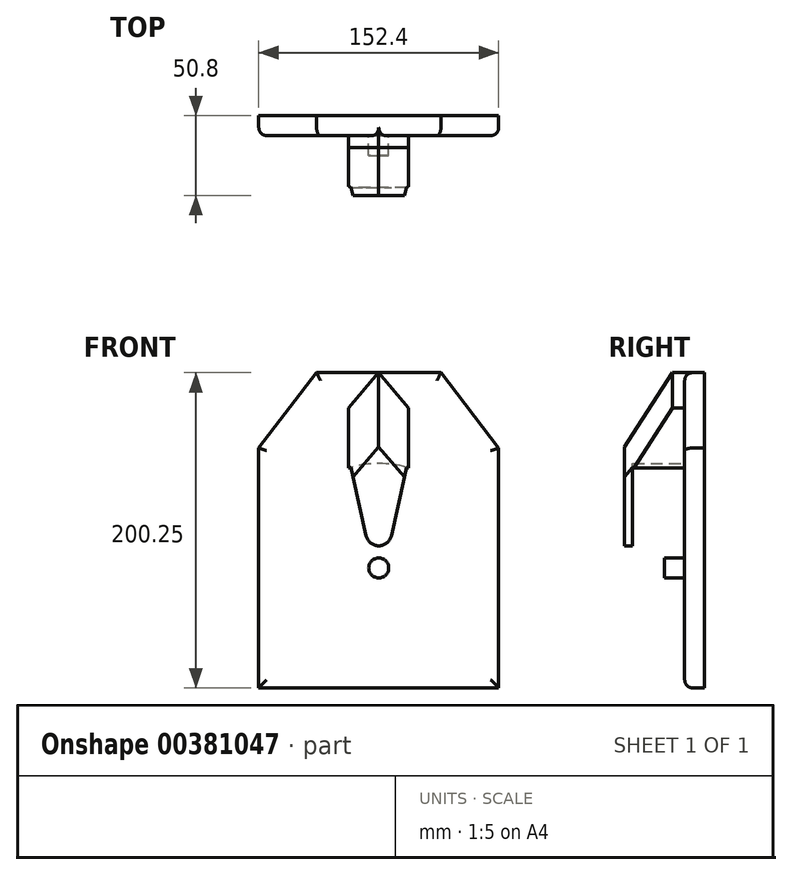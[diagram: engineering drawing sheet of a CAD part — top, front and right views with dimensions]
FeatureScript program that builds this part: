
annotation { "Feature Type Name" : "Feature", "Feature Type Description" : "" }
export const myFeature = defineFeature(function(context is Context, id is Id, definition is map)
    precondition{}
    {
        {
            var Q0;
            Q0=qCreatedBy(makeId("Front.planeOp"),FACE);
            var sketch = newSketch(context, id + "F0", { "sketchPlane" : qUnion([Q0])});
            skLineSegment(sketch, "E0.bottom", {"start": v(-76.2, 76.2) * mm, "end": v(76.2, 76.2) * mm});
            skLineSegment(sketch, "E0.top", {"start": v(-76.2, -76.2) * mm, "end": v(76.2, -76.2) * mm});
            skLineSegment(sketch, "E0.left", {"start": v(-76.2, 76.2) * mm, "end": v(-76.2, -76.2) * mm});
            skLineSegment(sketch, "E0.right", {"start": v(76.2, 76.2) * mm, "end": v(76.2, -76.2) * mm});
            skPoint(sketch, "E0.middle", {"position": v(0, 0) * mm});
            skLineSegment(sketch, "E1.bottom", {"start": v(-39.47, 124.05) * mm, "end": v(39.47, 124.05) * mm});
            skLineSegment(sketch, "E1.top", {"start": v(-39.47, 28.35) * mm, "end": v(39.47, 28.35) * mm});
            skLineSegment(sketch, "E1.left", {"start": v(-39.47, 124.05) * mm, "end": v(-39.47, 28.35) * mm});
            skLineSegment(sketch, "E1.right", {"start": v(39.47, 124.05) * mm, "end": v(39.47, 28.35) * mm});
            skPoint(sketch, "E1.middle", {"position": v(0, 76.2) * mm});
            skLineSegment(sketch, "E2", {"start": v(-39.47, 124.05) * mm, "end": v(-76.2, 76.2) * mm});
            skLineSegment(sketch, "E3", {"start": v(39.47, 124.05) * mm, "end": v(76.2, 76.2) * mm});
            skSolve(sketch);
        }
        {
            var Q0;
            Q0 = qSketchRegion(id + "F0", true);
            var Q1;
            {var subQ5=sQuery(id+"F0.wireOp",EDGE,"E1.top");Q1=makeQuery(id+"F0.imprint","IMPRINT",FACE,{"disambiguationData":[TD([[makeQuery(id+"F0.imprint","IMPRINT",EDGE,{"derivedFrom":subQ5}),1.0]])]});}
            extrude(context, id + "F1", {"entities" : qUnion([Q0, Q1]), "depth" : 12.7 * mm});
        }
        {
            var Q0;
            Q0=makeQuery(id+"F1.opExtrude","CAP_FACE",FACE,{"disambiguationData":[OSD([sQuery(id+"F0.wireOp",EDGE,"E0.bottom"),sQuery(id+"F0.wireOp",EDGE,"E0.top"),sQuery(id+"F0.wireOp",EDGE,"E0.left"),sQuery(id+"F0.wireOp",EDGE,"E0.right")])],"isStart":false});
            var sketch = newSketch(context, id + "F2", { "sketchPlane" : qUnion([Q0])});
            skCircle(sketch, "E4", {"center": v(0, 0) * mm, "radius": 6.35 * mm});
            skSolve(sketch);
        }
        {
            var Q0;
            Q0 = qSketchRegion(id + "F2", true);
            extrude(context, id + "F3", {"entities" : qUnion([Q0]), "operationType" : NewBodyOperationType.ADD, "depth" : 12.7 * mm});
        }
        {
            var Q0;
            Q0=makeQuery(id+"F1.opExtrude","CAP_FACE",FACE,{"disambiguationData":[OSD([sQuery(id+"F0.wireOp",EDGE,"E0.top"),sQuery(id+"F0.wireOp",EDGE,"E0.left"),sQuery(id+"F0.wireOp",EDGE,"E0.right"),sQuery(id+"F0.wireOp",EDGE,"E1.bottom"),sQuery(id+"F0.wireOp",EDGE,"E2"),sQuery(id+"F0.wireOp",EDGE,"E3")])],"isStart":false});
            var sketch = newSketch(context, id + "F4", { "sketchPlane" : qUnion([Q0])});
            skLineSegment(sketch, "E5.bottom", {"start": v(-19.05, 101.6) * mm, "end": v(19.05, 101.6) * mm});
            skLineSegment(sketch, "E5.top", {"start": v(-19.05, 63.5) * mm, "end": v(19.05, 63.5) * mm});
            skLineSegment(sketch, "E5.left", {"start": v(-19.05, 101.6) * mm, "end": v(-19.05, 63.5) * mm});
            skLineSegment(sketch, "E5.right", {"start": v(19.05, 101.6) * mm, "end": v(19.05, 63.5) * mm});
            skPoint(sketch, "E5.middle", {"position": v(0, 82.55) * mm});
            skLineSegment(sketch, "E6", {"start": v(0, 124.05) * mm, "end": v(19.05, 101.6) * mm});
            skLineSegment(sketch, "E7", {"start": v(0, 124.05) * mm, "end": v(-19.05, 101.6) * mm});
            skCircle(sketch, "E8", {"center": v(0, 0) * mm, "radius": 66.3 * mm});
            skSolve(sketch);
        }
        {
            var Q0;
            Q0=makeQuery(id+"F4.imprint","IMPRINT",FACE,{"disambiguationData":[TD([[makeQuery(id+"F4.imprint","IMPRINT",EDGE,{"derivedFrom":sQuery(id+"F4.wireOp",EDGE,"E5.bottom")}),1.0]])]});
            var Q1;
            Q1=makeQuery(id+"F4.imprint","IMPRINT",FACE,{"disambiguationData":[TD([[makeQuery(id+"F4.imprint","IMPRINT",EDGE,{"derivedFrom":sQuery(id+"F4.wireOp",EDGE,"E5.bottom")}),-1.0]])]});
            extrude(context, id + "F5", {"entities" : qUnion([Q0, Q1]), "operationType" : NewBodyOperationType.ADD, "depth" : 33.02 * mm});
        }
        {
            var Q0;
            Q0=makeQuery(id+"F5.opExtrude","CAP_EDGE",EDGE,{"disambiguationData":[OSD([sQuery(id+"F4.wireOp",EDGE,"E6")])],"isStart":false});
            var Q1;
            Q1=makeQuery(id+"F5.opExtrude","CAP_EDGE",EDGE,{"disambiguationData":[OSD([sQuery(id+"F4.wireOp",EDGE,"E7")])],"isStart":false});
            chamfer(context, id + "F6", {"entities" : qUnion([Q0, Q1]), "width" : 25.4 * mm, "tangentPropagation" : true});
        }
        {
            var Q0;
            Q0=makeQuery(id+"F5.opExtrude","CAP_FACE",FACE,{"disambiguationData":[OSD([sQuery(id+"F4.wireOp",EDGE,"E5.left"),sQuery(id+"F4.wireOp",EDGE,"E5.right"),sQuery(id+"F4.wireOp",EDGE,"E6"),sQuery(id+"F4.wireOp",EDGE,"E7"),sQuery(id+"F4.wireOp",EDGE,"E8")])],"isStart":false});
            var sketch = newSketch(context, id + "F7", { "sketchPlane" : qUnion([Q0])});
            skCircle(sketch, "E9", {"center": v(0, 22.23) * mm, "radius": 8.15 * mm});
            skPoint(sketch, "E9.centerSnap0", {"position": v(0, 66.3) * mm});
            skLineSegment(sketch, "E10", {"start": v(-17.75, 63.88) * mm, "end": v(-7.95, 20.43) * mm});
            skLineSegment(sketch, "E11", {"start": v(17.75, 63.88) * mm, "end": v(7.95, 20.43) * mm});
            skSolve(sketch);
        }
        {
            var Q0;
            Q0 = qSketchRegion(id + "F7", true);
            var Q1;
            {var subQ0=sQuery(id+"F7.wireOp",EDGE,"E10");Q1=makeQuery(id+"F7.imprint","IMPRINT",FACE,{"disambiguationData":[TD([[makeQuery(id+"F7.imprint","IMPRINT",EDGE,{"derivedFrom":subQ0}),1.0]])]});}
            var Q2;
            {var subQ0=sQuery(id+"F4.wireOp",EDGE,"E8");Q2=makeQuery(id+"F7.imprint","IMPRINT",FACE,{"disambiguationData":[TD([[makeQuery(id+"F7.imprint","IMPRINT",EDGE,{"derivedFrom":makeQuery(id+"F5.opExtrude","CAP_EDGE",EDGE,{"disambiguationData":[OSD([subQ0])],"isStart":false})}),-1.0]])]});}
            extrude(context, id + "F8", {"entities" : qUnion([Q0, Q1, Q2]), "operationType" : NewBodyOperationType.ADD, "depth" : 5.08 * mm});
        }
        {
            var Q0;
            {var subQ0=sQuery(id+"F4.wireOp",EDGE,"E8");var subQ1=sQuery(id+"F4.wireOp",EDGE,"E7");var subQ2=sQuery(id+"F4.wireOp",EDGE,"E6");var subQ3=sQuery(id+"F4.wireOp",EDGE,"E5.right");var subQ4=sQuery(id+"F4.wireOp",EDGE,"E5.left");Q0=makeQuery(id+"F8.opExtrude","CAP_EDGE",EDGE,{"disambiguationData":[OSD([subQ4,subQ3,subQ2,subQ1,subQ0]),TDD([makeQuery(id+"F7.imprint","IMPRINT",EDGE,{"derivedFrom":makeQuery(id+"F6.opChamfer","BLEND_EDGE",EDGE,{"blendedFrom":[makeQuery(id+"F5.opExtrude","CAP_EDGE",EDGE,{"disambiguationData":[OSD([subQ2])],"isStart":false}),makeQuery(id+"F5.opExtrude","CAP_FACE",FACE,{"disambiguationData":[OSD([subQ4,subQ3,subQ2,subQ1,subQ0])],"isStart":false})],"blendedInto":[makeQuery(id+"F5.opExtrude","CAP_FACE",FACE,{"disambiguationData":[OSD([subQ4,subQ3,subQ2,subQ1,subQ0])],"isStart":false})]})})])],"isStart":false});}
            var Q1;
            {var subQ0=sQuery(id+"F4.wireOp",EDGE,"E8");var subQ1=sQuery(id+"F4.wireOp",EDGE,"E7");var subQ2=sQuery(id+"F4.wireOp",EDGE,"E6");var subQ3=sQuery(id+"F4.wireOp",EDGE,"E5.right");var subQ4=sQuery(id+"F4.wireOp",EDGE,"E5.left");Q1=makeQuery(id+"F8.opExtrude","CAP_EDGE",EDGE,{"disambiguationData":[OSD([subQ4,subQ3,subQ2,subQ1,subQ0]),TDD([makeQuery(id+"F7.imprint","IMPRINT",EDGE,{"derivedFrom":makeQuery(id+"F6.opChamfer","BLEND_EDGE",EDGE,{"blendedFrom":[makeQuery(id+"F5.opExtrude","CAP_EDGE",EDGE,{"disambiguationData":[OSD([subQ1])],"isStart":false}),makeQuery(id+"F5.opExtrude","CAP_FACE",FACE,{"disambiguationData":[OSD([subQ4,subQ3,subQ2,subQ1,subQ0])],"isStart":false})],"blendedInto":[makeQuery(id+"F5.opExtrude","CAP_FACE",FACE,{"disambiguationData":[OSD([subQ4,subQ3,subQ2,subQ1,subQ0])],"isStart":false})]})})])],"isStart":false});}
            var Q2;
            Q2=makeQuery(id+"F5.opExtrude","CAP_EDGE",EDGE,{"disambiguationData":[OSD([sQuery(id+"F4.wireOp",EDGE,"E8")])],"isStart":false});
            chamfer(context, id + "F9", {"entities" : qUnion([Q0, Q1, Q2]), "width" : 5.08 * mm, "tangentPropagation" : true});
        }
        {
            var Q0;
            Q0=makeQuery(id+"F1.opExtrude","CAP_EDGE",EDGE,{"disambiguationData":[OSD([sQuery(id+"F0.wireOp",EDGE,"E3")])],"isStart":false});
            var Q1;
            Q1=makeQuery(id+"F1.opExtrude","CAP_EDGE",EDGE,{"disambiguationData":[OSD([sQuery(id+"F0.wireOp",EDGE,"E0.right")])],"isStart":false});
            var Q2;
            {var subQ0=sQuery(id+"F0.wireOp",EDGE,"E1.bottom");var subQ1=sQuery(id+"F0.wireOp",EDGE,"E3");Q2=makeQuery(id+"F5.boolean.opBoolean","SPLIT",EDGE,{"disambiguationData":[TD([makeQuery(id+"F1.opExtrude","SWEPT_FACE",FACE,{"disambiguationData":[OSD([subQ1])]})])],"derivedFrom":makeQuery(id+"F1.opExtrude","CAP_EDGE",EDGE,{"disambiguationData":[OSD([subQ0])],"isStart":false})});}
            var Q3;
            {var subQ0=sQuery(id+"F0.wireOp",EDGE,"E2");var subQ1=sQuery(id+"F0.wireOp",EDGE,"E1.bottom");Q3=makeQuery(id+"F5.boolean.opBoolean","SPLIT",EDGE,{"disambiguationData":[TD([makeQuery(id+"F1.opExtrude","SWEPT_FACE",FACE,{"disambiguationData":[OSD([subQ0])]})])],"derivedFrom":makeQuery(id+"F1.opExtrude","CAP_EDGE",EDGE,{"disambiguationData":[OSD([subQ1])],"isStart":false})});}
            var Q4;
            Q4=makeQuery(id+"F1.opExtrude","CAP_EDGE",EDGE,{"disambiguationData":[OSD([sQuery(id+"F0.wireOp",EDGE,"E2")])],"isStart":false});
            var Q5;
            Q5=makeQuery(id+"F1.opExtrude","CAP_EDGE",EDGE,{"disambiguationData":[OSD([sQuery(id+"F0.wireOp",EDGE,"E0.left")])],"isStart":false});
            var Q6;
            Q6=makeQuery(id+"F1.opExtrude","CAP_EDGE",EDGE,{"disambiguationData":[OSD([sQuery(id+"F0.wireOp",EDGE,"E0.top")])],"isStart":false});
            fillet(context, id + "F10", {"entities" : qUnion([Q0, Q1, Q2, Q3, Q4, Q5, Q6]), "radius" : 5.08 * mm, "tangentPropagation" : true, "allowEdgeOverflow" : false});
        }
    });
